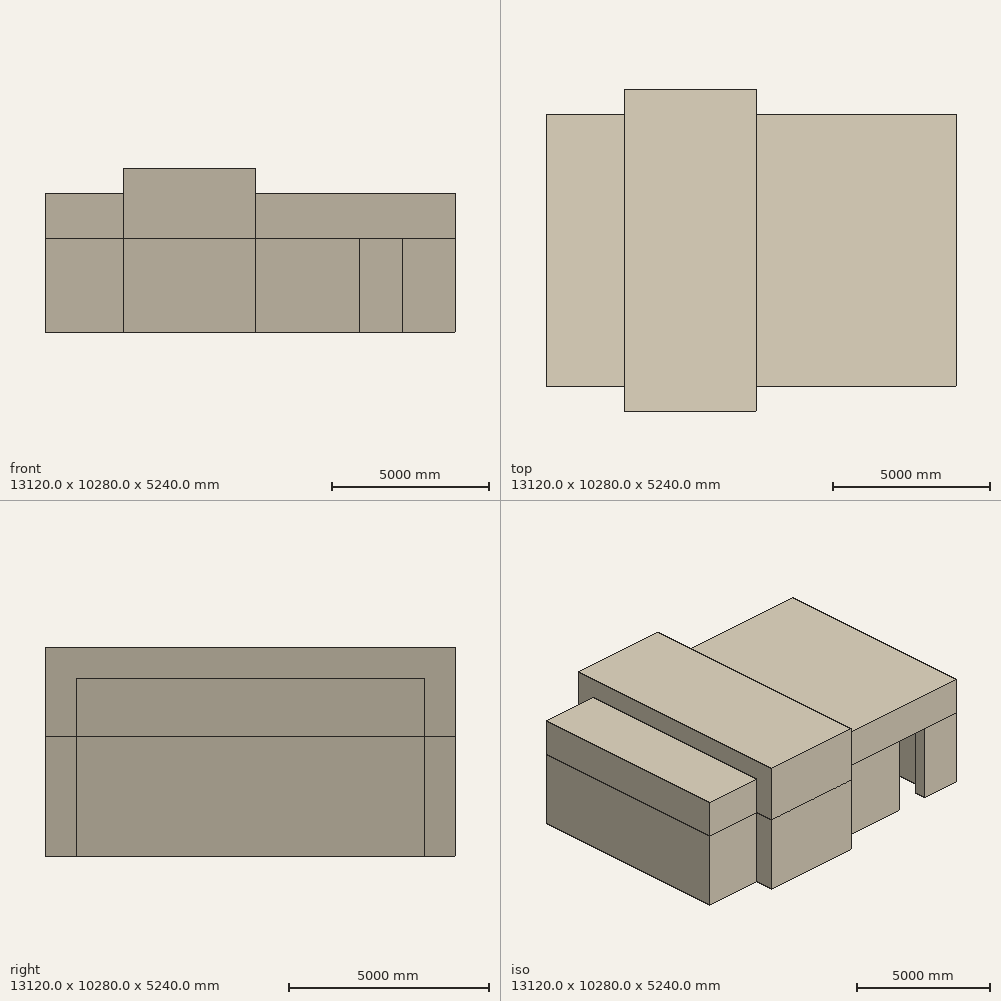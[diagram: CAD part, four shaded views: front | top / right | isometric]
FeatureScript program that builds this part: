
annotation { "Feature Type Name" : "Feature", "Feature Type Description" : "" }
export const myFeature = defineFeature(function(context is Context, id is Id, definition is map)
    precondition{}
    {
        {
            var Q0;
            Q0=qCreatedBy(makeId("Top.planeOp"),FACE);
            var sketch = newSketch(context, id + "F0", { "sketchPlane" : qUnion([Q0])});
            skLineSegment(sketch, "E0.bottom", {"start": v(3400, 2900) * mm, "end": v(-3400, 2900) * mm});
            skLineSegment(sketch, "E0.top", {"start": v(3400, -2900) * mm, "end": v(-3400, -2900) * mm});
            skLineSegment(sketch, "E0.left", {"start": v(3400, 2900) * mm, "end": v(3400, -2900) * mm});
            skLineSegment(sketch, "E0.right", {"start": v(-3400, 2900) * mm, "end": v(-3400, -2900) * mm});
            skPoint(sketch, "E0.middle", {"position": v(0, 0) * mm});
            skLineSegment(sketch, "E1.bottom", {"start": v(-4780, 4350) * mm, "end": v(8340, 4350) * mm});
            skLineSegment(sketch, "E1.top", {"start": v(-4780, -4350) * mm, "end": v(8340, -4350) * mm});
            skLineSegment(sketch, "E1.left", {"start": v(-4780, 4350) * mm, "end": v(-4780, -4350) * mm});
            skLineSegment(sketch, "E1.right", {"start": v(8340, 4350) * mm, "end": v(8340, -4350) * mm});
            skSolve(sketch);
        }
        {
            var Q0;
            Q0 = qSketchRegion(id + "F0", true);
            extrude(context, id + "F1", {"entities" : qUnion([Q0]), "depth" : 3000 * mm, "offsetDistance" : 25 * mm});
        }
        {
            var Q0;
            Q0=makeQuery(id+"F1.opExtrude","CAP_FACE",FACE,{"disambiguationData":[OSD([sQuery(id+"F0.wireOp",EDGE,"E0.bottom"),sQuery(id+"F0.wireOp",EDGE,"E0.top"),sQuery(id+"F0.wireOp",EDGE,"E0.left"),sQuery(id+"F0.wireOp",EDGE,"E0.right"),sQuery(id+"F0.wireOp",EDGE,"E1.bottom"),sQuery(id+"F0.wireOp",EDGE,"E1.top"),sQuery(id+"F0.wireOp",EDGE,"E1.left"),sQuery(id+"F0.wireOp",EDGE,"E1.right")])],"isStart":false});
            var sketch = newSketch(context, id + "F2", { "sketchPlane" : qUnion([Q0])});
            skLineSegment(sketch, "E2.bottom", {"start": v(-2280, 4350) * mm, "end": v(1940, 4350) * mm});
            skLineSegment(sketch, "E2.top", {"start": v(-2280, 5140) * mm, "end": v(1940, 5140) * mm});
            skLineSegment(sketch, "E2.left", {"start": v(-2280, 4350) * mm, "end": v(-2280, 5140) * mm});
            skLineSegment(sketch, "E2.right", {"start": v(1940, 4350) * mm, "end": v(1940, 5140) * mm});
            skLineSegment(sketch, "E3", {"start": v(8340, 0) * mm, "end": v(-4780, 0) * mm, "construction": true});
            skLineSegment(sketch, "E4.MirrorCS", {"start": v(-2280, -4350) * mm, "end": v(1940, -4350) * mm});
            skLineSegment(sketch, "E5.MirrorCS", {"start": v(-2280, -5140) * mm, "end": v(1940, -5140) * mm});
            skLineSegment(sketch, "E6.MirrorCS", {"start": v(-2280, -4350) * mm, "end": v(-2280, -5140) * mm});
            skLineSegment(sketch, "E7.MirrorCS", {"start": v(1940, -4350) * mm, "end": v(1940, -5140) * mm});
            skSolve(sketch);
        }
        {
            var Q0;
            Q0 = qSketchRegion(id + "F2", true);
            var Q1;
            Q1=makeQuery(id+"F1.opExtrude","CAP_VERTEX",VERTEX,{"disambiguationData":[OSD([sQuery(id+"F0.wireOp",EDGE,"E1.top"),sQuery(id+"F0.wireOp",EDGE,"E1.right")])],"isStart":true});
            extrude(context, id + "F3", {"entities" : qUnion([Q0]), "operationType" : NewBodyOperationType.ADD, "endBound" : BoundingType.UP_TO_VERTEX, "oppositeDirection" : true, "depth" : 25 * mm, "endBoundEntityVertex" : qUnion([Q1]), "offsetDistance" : 25 * mm});
        }
        {
            var Q0;
            Q0=makeQuery(id+"F3.boolean.opBoolean","MERGE",FACE,{"derivedFrom":[makeQuery(id+"F1.opExtrude","CAP_FACE",FACE,{"disambiguationData":[OSD([sQuery(id+"F0.wireOp",EDGE,"E0.bottom"),sQuery(id+"F0.wireOp",EDGE,"E0.top"),sQuery(id+"F0.wireOp",EDGE,"E0.left"),sQuery(id+"F0.wireOp",EDGE,"E0.right"),sQuery(id+"F0.wireOp",EDGE,"E1.bottom"),sQuery(id+"F0.wireOp",EDGE,"E1.top"),sQuery(id+"F0.wireOp",EDGE,"E1.left"),sQuery(id+"F0.wireOp",EDGE,"E1.right")])],"isStart":false}),makeQuery(id+"F3.opExtrude","CAP_FACE",FACE,{"disambiguationData":[OSD([sQuery(id+"F2.wireOp",EDGE,"E2.bottom"),sQuery(id+"F2.wireOp",EDGE,"E2.top"),sQuery(id+"F2.wireOp",EDGE,"E2.left"),sQuery(id+"F2.wireOp",EDGE,"E2.right")])],"isStart":true}),makeQuery(id+"F3.opExtrude","CAP_FACE",FACE,{"disambiguationData":[OSD([sQuery(id+"F2.wireOp",EDGE,"E4.MirrorCS"),sQuery(id+"F2.wireOp",EDGE,"E5.MirrorCS"),sQuery(id+"F2.wireOp",EDGE,"E6.MirrorCS"),sQuery(id+"F2.wireOp",EDGE,"E7.MirrorCS")])],"isStart":true})]});
            var sketch = newSketch(context, id + "F4", { "sketchPlane" : qUnion([Q0])});
            skLineSegment(sketch, "E8", {"start": v(4780, -3850) * mm, "end": v(4780, 2900) * mm});
            skLineSegment(sketch, "E9", {"start": v(4780, 2900) * mm, "end": v(7150, 2900) * mm});
            skLineSegment(sketch, "E10", {"start": v(7150, 2900) * mm, "end": v(7150, -3850) * mm});
            skLineSegment(sketch, "E11", {"start": v(6650, -3850) * mm, "end": v(7150, -3850) * mm});
            skLineSegment(sketch, "E12", {"start": v(6650, -3850) * mm, "end": v(6650, -4350) * mm});
            skLineSegment(sketch, "E13", {"start": v(3400, 2900) * mm, "end": v(4780, 2900) * mm, "construction": true});
            skLineSegment(sketch, "E14", {"start": v(4780, -3850) * mm, "end": v(5280, -3850) * mm});
            skLineSegment(sketch, "E15", {"start": v(5280, -3850) * mm, "end": v(5280, -4350) * mm});
            skLineSegment(sketch, "E16", {"start": v(5280, -4350) * mm, "end": v(6650, -4350) * mm});
            skSolve(sketch);
        }
        {
            var Q0;
            Q0 = qSketchRegion(id + "F4", true);
            extrude(context, id + "F5", {"entities" : qUnion([Q0]), "operationType" : NewBodyOperationType.REMOVE, "endBound" : BoundingType.THROUGH_ALL, "oppositeDirection" : true, "depth" : 25 * mm, "offsetDistance" : 25 * mm});
        }
        {
            var Q0;
            Q0=makeQuery(id+"F3.boolean.opBoolean","MERGE",FACE,{"derivedFrom":[makeQuery(id+"F1.opExtrude","CAP_FACE",FACE,{"disambiguationData":[OSD([sQuery(id+"F0.wireOp",EDGE,"E0.bottom"),sQuery(id+"F0.wireOp",EDGE,"E0.top"),sQuery(id+"F0.wireOp",EDGE,"E0.left"),sQuery(id+"F0.wireOp",EDGE,"E0.right"),sQuery(id+"F0.wireOp",EDGE,"E1.bottom"),sQuery(id+"F0.wireOp",EDGE,"E1.top"),sQuery(id+"F0.wireOp",EDGE,"E1.left"),sQuery(id+"F0.wireOp",EDGE,"E1.right")])],"isStart":false}),makeQuery(id+"F3.opExtrude","CAP_FACE",FACE,{"disambiguationData":[OSD([sQuery(id+"F2.wireOp",EDGE,"E2.bottom"),sQuery(id+"F2.wireOp",EDGE,"E2.top"),sQuery(id+"F2.wireOp",EDGE,"E2.left"),sQuery(id+"F2.wireOp",EDGE,"E2.right")])],"isStart":true}),makeQuery(id+"F3.opExtrude","CAP_FACE",FACE,{"disambiguationData":[OSD([sQuery(id+"F2.wireOp",EDGE,"E4.MirrorCS"),sQuery(id+"F2.wireOp",EDGE,"E5.MirrorCS"),sQuery(id+"F2.wireOp",EDGE,"E6.MirrorCS"),sQuery(id+"F2.wireOp",EDGE,"E7.MirrorCS")])],"isStart":true})]});
            var sketch = newSketch(context, id + "F6", { "sketchPlane" : qUnion([Q0])});
            skLineSegment(sketch, "E17.bottom", {"start": v(3400, 2900) * mm, "end": v(4780, 2900) * mm});
            skLineSegment(sketch, "E17.top", {"start": v(3400, 530) * mm, "end": v(4780, 530) * mm});
            skLineSegment(sketch, "E17.left", {"start": v(3400, 2900) * mm, "end": v(3400, 530) * mm});
            skLineSegment(sketch, "E17.right", {"start": v(4780, 2900) * mm, "end": v(4780, 530) * mm});
            skLineSegment(sketch, "E18.0", {"start": v(4780, 2900) * mm, "end": v(7150, 2900) * mm, "construction": true});
            skSolve(sketch);
        }
        {
            var Q0;
            Q0 = qSketchRegion(id + "F6", true);
            extrude(context, id + "F7", {"entities" : qUnion([Q0]), "operationType" : NewBodyOperationType.REMOVE, "endBound" : BoundingType.THROUGH_ALL, "oppositeDirection" : true, "depth" : 25 * mm, "offsetDistance" : 25 * mm});
        }
        {
            var Q0;
            Q0=makeQuery(id+"F3.boolean.opBoolean","MERGE",FACE,{"derivedFrom":[makeQuery(id+"F1.opExtrude","CAP_FACE",FACE,{"disambiguationData":[OSD([sQuery(id+"F0.wireOp",EDGE,"E0.bottom"),sQuery(id+"F0.wireOp",EDGE,"E0.top"),sQuery(id+"F0.wireOp",EDGE,"E0.left"),sQuery(id+"F0.wireOp",EDGE,"E0.right"),sQuery(id+"F0.wireOp",EDGE,"E1.bottom"),sQuery(id+"F0.wireOp",EDGE,"E1.top"),sQuery(id+"F0.wireOp",EDGE,"E1.left"),sQuery(id+"F0.wireOp",EDGE,"E1.right")])],"isStart":false}),makeQuery(id+"F3.opExtrude","CAP_FACE",FACE,{"disambiguationData":[OSD([sQuery(id+"F2.wireOp",EDGE,"E2.bottom"),sQuery(id+"F2.wireOp",EDGE,"E2.top"),sQuery(id+"F2.wireOp",EDGE,"E2.left"),sQuery(id+"F2.wireOp",EDGE,"E2.right")])],"isStart":true}),makeQuery(id+"F3.opExtrude","CAP_FACE",FACE,{"disambiguationData":[OSD([sQuery(id+"F2.wireOp",EDGE,"E4.MirrorCS"),sQuery(id+"F2.wireOp",EDGE,"E5.MirrorCS"),sQuery(id+"F2.wireOp",EDGE,"E6.MirrorCS"),sQuery(id+"F2.wireOp",EDGE,"E7.MirrorCS")])],"isStart":true})]});
            var sketch = newSketch(context, id + "F8", { "sketchPlane" : qUnion([Q0])});
            skLineSegment(sketch, "E19.bottom", {"start": v(3400, 530) * mm, "end": v(2900, 530) * mm});
            skLineSegment(sketch, "E19.top", {"start": v(3400, 30) * mm, "end": v(2900, 30) * mm});
            skLineSegment(sketch, "E19.left", {"start": v(3400, 530) * mm, "end": v(3400, 30) * mm});
            skLineSegment(sketch, "E19.right", {"start": v(2900, 530) * mm, "end": v(2900, 30) * mm});
            skSolve(sketch);
        }
        {
            var Q0;
            Q0 = qSketchRegion(id + "F8", true);
            var Q1;
            Q1=makeQuery(id+"F1.opExtrude","CAP_VERTEX",VERTEX,{"disambiguationData":[OSD([sQuery(id+"F0.wireOp",EDGE,"E1.top"),sQuery(id+"F0.wireOp",EDGE,"E1.right")])],"isStart":true});
            extrude(context, id + "F9", {"entities" : qUnion([Q0]), "operationType" : NewBodyOperationType.ADD, "endBound" : BoundingType.UP_TO_VERTEX, "oppositeDirection" : true, "depth" : 25 * mm, "endBoundEntityVertex" : qUnion([Q1]), "offsetDistance" : 25 * mm});
        }
        {
            var Q0;
            Q0=makeQuery(id+"F9.boolean.opBoolean","MERGE",FACE,{"derivedFrom":[makeQuery(id+"F3.boolean.opBoolean","MERGE",FACE,{"derivedFrom":[makeQuery(id+"F1.opExtrude","CAP_FACE",FACE,{"disambiguationData":[OSD([sQuery(id+"F0.wireOp",EDGE,"E0.bottom"),sQuery(id+"F0.wireOp",EDGE,"E0.top"),sQuery(id+"F0.wireOp",EDGE,"E0.left"),sQuery(id+"F0.wireOp",EDGE,"E0.right"),sQuery(id+"F0.wireOp",EDGE,"E1.bottom"),sQuery(id+"F0.wireOp",EDGE,"E1.top"),sQuery(id+"F0.wireOp",EDGE,"E1.left"),sQuery(id+"F0.wireOp",EDGE,"E1.right")])],"isStart":false}),makeQuery(id+"F3.opExtrude","CAP_FACE",FACE,{"disambiguationData":[OSD([sQuery(id+"F2.wireOp",EDGE,"E2.bottom"),sQuery(id+"F2.wireOp",EDGE,"E2.top"),sQuery(id+"F2.wireOp",EDGE,"E2.left"),sQuery(id+"F2.wireOp",EDGE,"E2.right")])],"isStart":true}),makeQuery(id+"F3.opExtrude","CAP_FACE",FACE,{"disambiguationData":[OSD([sQuery(id+"F2.wireOp",EDGE,"E4.MirrorCS"),sQuery(id+"F2.wireOp",EDGE,"E5.MirrorCS"),sQuery(id+"F2.wireOp",EDGE,"E6.MirrorCS"),sQuery(id+"F2.wireOp",EDGE,"E7.MirrorCS")])],"isStart":true})]}),makeQuery(id+"F9.opExtrude","CAP_FACE",FACE,{"disambiguationData":[OSD([sQuery(id+"F8.wireOp",EDGE,"E19.bottom"),sQuery(id+"F8.wireOp",EDGE,"E19.top"),sQuery(id+"F8.wireOp",EDGE,"E19.left"),sQuery(id+"F8.wireOp",EDGE,"E19.right")])],"isStart":true})]});
            var sketch = newSketch(context, id + "F10", { "sketchPlane" : qUnion([Q0])});
            skLineSegment(sketch, "E20", {"start": v(-4780, 4350) * mm, "end": v(-4780, -4350) * mm});
            skLineSegment(sketch, "E21", {"start": v(-4780, -4350) * mm, "end": v(-2280, -4350) * mm});
            skLineSegment(sketch, "E22", {"start": v(-2280, -4350) * mm, "end": v(-2280, -5140) * mm});
            skLineSegment(sketch, "E23", {"start": v(-2280, -5140) * mm, "end": v(1940, -5140) * mm});
            skLineSegment(sketch, "E24", {"start": v(1940, -5140) * mm, "end": v(1940, -4350) * mm});
            skLineSegment(sketch, "E25", {"start": v(1940, -4350) * mm, "end": v(8340, -4350) * mm});
            skLineSegment(sketch, "E26", {"start": v(8340, -4350) * mm, "end": v(8340, 4350) * mm});
            skLineSegment(sketch, "E27", {"start": v(8340, 4350) * mm, "end": v(1940, 4350) * mm});
            skLineSegment(sketch, "E28", {"start": v(1940, 4350) * mm, "end": v(1940, 5140) * mm});
            skLineSegment(sketch, "E29", {"start": v(1940, 5140) * mm, "end": v(-2280, 5140) * mm});
            skLineSegment(sketch, "E30", {"start": v(-2280, 5140) * mm, "end": v(-2280, 4350) * mm});
            skLineSegment(sketch, "E31", {"start": v(-2280, 4350) * mm, "end": v(-4780, 4350) * mm});
            skSolve(sketch);
        }
        {
            var Q0;
            Q0 = qSketchRegion(id + "F10", true);
            extrude(context, id + "F11", {"entities" : qUnion([Q0]), "depth" : 1450 * mm, "offsetDistance" : 25 * mm});
        }
        {
            var Q0;
            Q0=makeQuery(id+"F11.opExtrude","CAP_FACE",FACE,{"disambiguationData":[OSD([sQuery(id+"F10.wireOp",EDGE,"E20"),sQuery(id+"F10.wireOp",EDGE,"E21"),sQuery(id+"F10.wireOp",EDGE,"E22"),sQuery(id+"F10.wireOp",EDGE,"E23"),sQuery(id+"F10.wireOp",EDGE,"E24"),sQuery(id+"F10.wireOp",EDGE,"E25"),sQuery(id+"F10.wireOp",EDGE,"E26"),sQuery(id+"F10.wireOp",EDGE,"E27"),sQuery(id+"F10.wireOp",EDGE,"E28"),sQuery(id+"F10.wireOp",EDGE,"E29"),sQuery(id+"F10.wireOp",EDGE,"E30"),sQuery(id+"F10.wireOp",EDGE,"E31")])],"isStart":false});
            var sketch = newSketch(context, id + "F12", { "sketchPlane" : qUnion([Q0])});
            skLineSegment(sketch, "E32.bottom", {"start": v(-2280, 5140) * mm, "end": v(1940, 5140) * mm});
            skLineSegment(sketch, "E32.top", {"start": v(-2280, -5140) * mm, "end": v(1940, -5140) * mm});
            skLineSegment(sketch, "E32.left", {"start": v(-2280, 5140) * mm, "end": v(-2280, -5140) * mm});
            skLineSegment(sketch, "E32.right", {"start": v(1940, 5140) * mm, "end": v(1940, -5140) * mm});
            skSolve(sketch);
        }
        {
            var Q0;
            Q0 = qSketchRegion(id + "F12", true);
            extrude(context, id + "F13", {"entities" : qUnion([Q0]), "operationType" : NewBodyOperationType.ADD, "depth" : 790 * mm, "offsetDistance" : 25 * mm});
        }
    });
